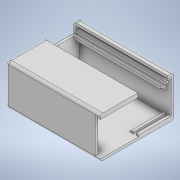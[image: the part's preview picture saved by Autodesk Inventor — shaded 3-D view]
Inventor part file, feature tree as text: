
AUTODESK INVENTOR PART (.ipt)
format: ipt  version: 2020 (Build 240168000, 168)  size: 850,944 bytes
history: native  units: in
note: dims shown in document units (in); Inventor stores cm internally (conversion verified against a paired STEP export)
features: extrude x40, sketch x36, projected_geometry x31, move_body x3, plane x2, split x2, boolean_combine x2, chamfer x2, fillet x1, mirror x1
ambient origin geometry x8: Origin, YZ Plane, XZ Plane, XY Plane, X Axis, Y Axis, Z Axis, Center Point
bodies: Solid1 (feature_tree), Solid2 (feature_tree), Solid3 (feature_tree), Solid4 (feature_tree), Solid6 (feature_tree), Solid7 (feature_tree)
feature tree (120):
  sketch  "Sketch1"  dims[d0=4.3307in d1=2.1654in]
  extrude  "Extrusion1"  Depth=4.3307in
  extrude  "Extrusion2"  Depth=1.5748in
  extrude  "Extrusion3"  Depth=0.1181in TaperAngle=0.0deg
  extrude  "Extrusion4"  Depth=0.1181in TaperAngle=0.0deg
  extrude  "Extrusion5"  Depth=0.315in
  extrude  "Extrusion6"  Depth=0.1181in TaperAngle=0.0deg
  extrude  "Extrusion7"  Depth=0.0787in
  fillet  "Fillet2"  Radius=0.0394in
  extrude  "Extrusion8"  Depth=0.5906in
  extrude  "Extrusion10"  Depth=0.4724in
  extrude  "Extrusion11"  Depth=1.1417in
  mirror  "Mirror1"
  extrude  "Extrusion12"  Depth=0.1575in TaperAngle=0.0deg
  sketch  "Sketch14"  dims[d31=0.1181in d32=0.1575in d33=0.0in]
  extrude  "Extrusion13"  Depth=0.4724in
  extrude  "Extrusion14"  Depth=0.3937in TaperAngle=0.0deg
  extrude  "Extrusion15"  Depth=0.2756in
  sketch  "Sketch18"  dims[d47=0.1969in d48=0.2756in d49=0.0in]
  extrude  "Extrusion16"  Depth=0.2756in TaperAngle=0.0deg
  extrude  "Extrusion17"  Depth=0.1969in TaperAngle=0.0deg
  extrude  "Extrusion18"  Depth=0.1181in
  extrude  "Extrusion19"  Depth=0.0591in
  extrude  "Extrusion20"  Depth=0.3543in TaperAngle=0.0deg
  extrude  "Extrusion21"  Depth=0.2756in TaperAngle=0.0deg
  extrude  "Extrusion24"  Depth=1.378in
  extrude  "Extrusion25"  Depth=0.2362in TaperAngle=0.0deg
  extrude  "Extrusion26"  Depth=0.0787in TaperAngle=0.0deg
  extrude  "Extrusion27"  Depth=0.1181in
  extrude  "Extrusion28"  Depth=0.4724in TaperAngle=0.0deg
  plane  "Work Plane1"
  split  "Split1"
  move_body  "Move Body1"
  move_body  "Move Body2"
  extrude  "Extrusion30"  Depth=0.374in TaperAngle=0.0deg
  boolean_combine  "Combine1"
  extrude  "Extrusion31"  TaperAngle=0.0deg  [1 undecoded]
  extrude  "Extrusion32"  Depth=0.0787in TaperAngle=0.0deg
  extrude  "Extrusion33"  Depth=0.7338in TaperAngle=0.0deg
  extrude  "Extrusion34"  Depth=0.1181in
  chamfer  "Chamfer7"  Distance=0.0787in
  extrude  "Extrusion35"  Depth=0.1181in
  extrude  "Extrusion36"  Depth=0.0787in TaperAngle=45.0deg
  extrude  "Extrusion37"  Depth=0.0787in
  extrude  "Extrusion38"  Depth=0.1181in
  extrude  "Extrusion39"  Depth=0.0787in TaperAngle=0.0deg
  extrude  "Extrusion40"  Depth=0.0787in TaperAngle=0.0deg
  extrude  "Extrusion41"  Depth=0.0787in TaperAngle=0.0deg
  chamfer  "Chamfer10"  Distance=0.1575in
  sketch  "Sketch43"  dims[d145=0.0787in d146=0.0in d153=0.1181in]
  plane  "Work Plane3"
  split  "Split3"
  move_body  "Move Body4"
  boolean_combine  "Combine3"
  extrude  "Extrusion42"  Depth=0.0394in TaperAngle=0.0deg
  sketch  "Sketch45"  dims[d160=0.0787in d161=0.0in d162=0.0787in d163=0.0in d164=0.0787in d165=0.0in d166=0.1575in d167=0.0in d168=0.0394in d169=0.0in d170=0.1969in d171=0.0787in d172=45.0deg d173=0.0in d174=-0.1181in d175=0.0in d176=0.0in d177=0.1688in d178=0.0in d179=0.3543in d180=0.0in d181=0.4724in d182=0.0in d115=0.0197in d116=0.0344in]
  extrude  "Extrusion43"  Depth=0.1969in TaperAngle=45.0deg
  extrude  "Extrusion44"  TaperAngle=0.0deg  [1 undecoded]
  sketch  "Sketch4"  dims[d2=3.1496in d3=1.5748in]
  projected_geometry  "Projected Loop1"
  sketch  "Sketch5"  dims[d4=0.1181in d5=0.1181in d6=0.0in]
  sketch  "Sketch6"  dims[d7=1.7717in d8=0.0in d9=0.1181in d10=0.0in]
  projected_geometry  "Projected Loop2"
  sketch  "Sketch7"  dims[d11=0.1575in d12=0.315in]
  sketch  "Sketch8"  dims[d13=1.378in d14=0.1181in d15=0.0in]
  sketch  "Sketch9"  dims[d16=0.1575in d17=0.0in d18=0.0787in d19=0.0394in]
  sketch  "Sketch11"  dims[d20=0.2362in d21=0.0in d23=0.5906in]
  projected_geometry  "Projected Loop3"
  sketch  "Sketch12"  dims[d25=0.5906in d26=0.4724in]
  projected_geometry  "Projected Loop4"
  sketch  "Sketch13"  dims[d28=1.063in d29=1.1417in]
  sketch  "Sketch15"  dims[d35=0.1181in d36=0.4724in]
  sketch  "Sketch16"  dims[d37=0.4724in d39=0.3937in d40=0.0in]
  projected_geometry  "Projected Loop5"
  sketch  "Sketch17"  dims[d44=0.2756in d45=0.0in d46=0.4331in]
  projected_geometry  "Projected Loop6"
  projected_geometry  "Projected Loop7"
  sketch  "Sketch19"  dims[d53=3.3465in d54=0.0in d55=0.1969in d56=0.0in]
  projected_geometry  "Projected Loop8"
  sketch  "Sketch21"  dims[d60=0.0591in d61=0.1181in]
  sketch  "Sketch25"  dims[d62=0.1181in d63=0.0in d64=0.0591in]
  sketch  "Sketch26"  dims[d65=0.1181in d66=0.3543in d67=0.0in]
  projected_geometry  "Projected Loop11"
  projected_geometry  "Projected Loop12"
  sketch  "Sketch27"  dims[d69=0.9843in d70=0.2756in d71=0.0in]
  sketch  "Sketch28"  dims[d72=0.1181in d73=0.0in d78=1.378in]
  projected_geometry  "Projected Loop13"
  sketch  "Sketch30"  dims[d79=0.8661in d80=0.0in d81=0.2362in d82=0.0in]
  projected_geometry  "Projected Loop14"
  sketch  "Sketch31"  dims[d83=0.1181in d84=0.0787in d85=0.0in]
  sketch  "Sketch32"  dims[d86=0.2362in d87=0.0in d96=0.1181in]
  projected_geometry  "Projected Loop15"
  sketch  "Sketch33"  dims[d99=0.0787in d100=0.0in d101=0.4724in d102=0.0in]
  projected_geometry  "Projected Loop16"
  sketch  "Sketch34"  dims[d103=0.3937in d104=0.0in d111=0.374in d112=0.0in]
  projected_geometry  "Projected Loop17"
  sketch  "Sketch35"  dims[d113=0.096in d114=0.0in d120=0.0in]
  projected_geometry  "Projected Loop18"
  sketch  "Sketch36"  dims[d121=0.3937in d122=0.0in d123=0.0in d124=0.0787in d125=0.0in d126=0.0in]
  projected_geometry  "Projected Loop19"
  sketch  "Sketch38"  dims[d127=0.5187in d128=0.0in d129=0.7338in d130=0.0in]
  projected_geometry  "Projected Loop20"
  projected_geometry  "Projected Loop21"
  sketch  "Sketch39"  dims[d131=0.4724in d132=0.0in d133=0.1181in d134=0.0787in d135=0.0in]
  projected_geometry  "Projected Loop22"
  projected_geometry  "Projected Loop23"
  sketch  "Sketch40"  dims[d136=0.1181in d137=0.1181in]
  projected_geometry  "Projected Loop24"
  projected_geometry  "Projected Loop25"
  sketch  "Sketch41"  dims[d138=0.0787in d139=0.0in d140=0.0787in d141=0.0787in d142=45.0deg]
  projected_geometry  "Projected Loop26"
  projected_geometry  "Projected Loop27"
  sketch  "Sketch42"  dims[d143=0.1181in d144=0.0787in]
  projected_geometry  "Projected Loop28"
  projected_geometry  "Projected Loop29"
  projected_geometry  "Projected Loop30"
  sketch  "Sketch44"  dims[d154=0.1575in d155=0.0787in d156=0.0in]
  projected_geometry  "Projected Loop31"
  projected_geometry  "Projected Loop32"
  projected_geometry  "Projected Loop33"
note: 2 required parameter values undecoded (feature->parameter linkage not recoverable at this tier; creation-order binding heuristic only, values carry confidence <= 0.55)
